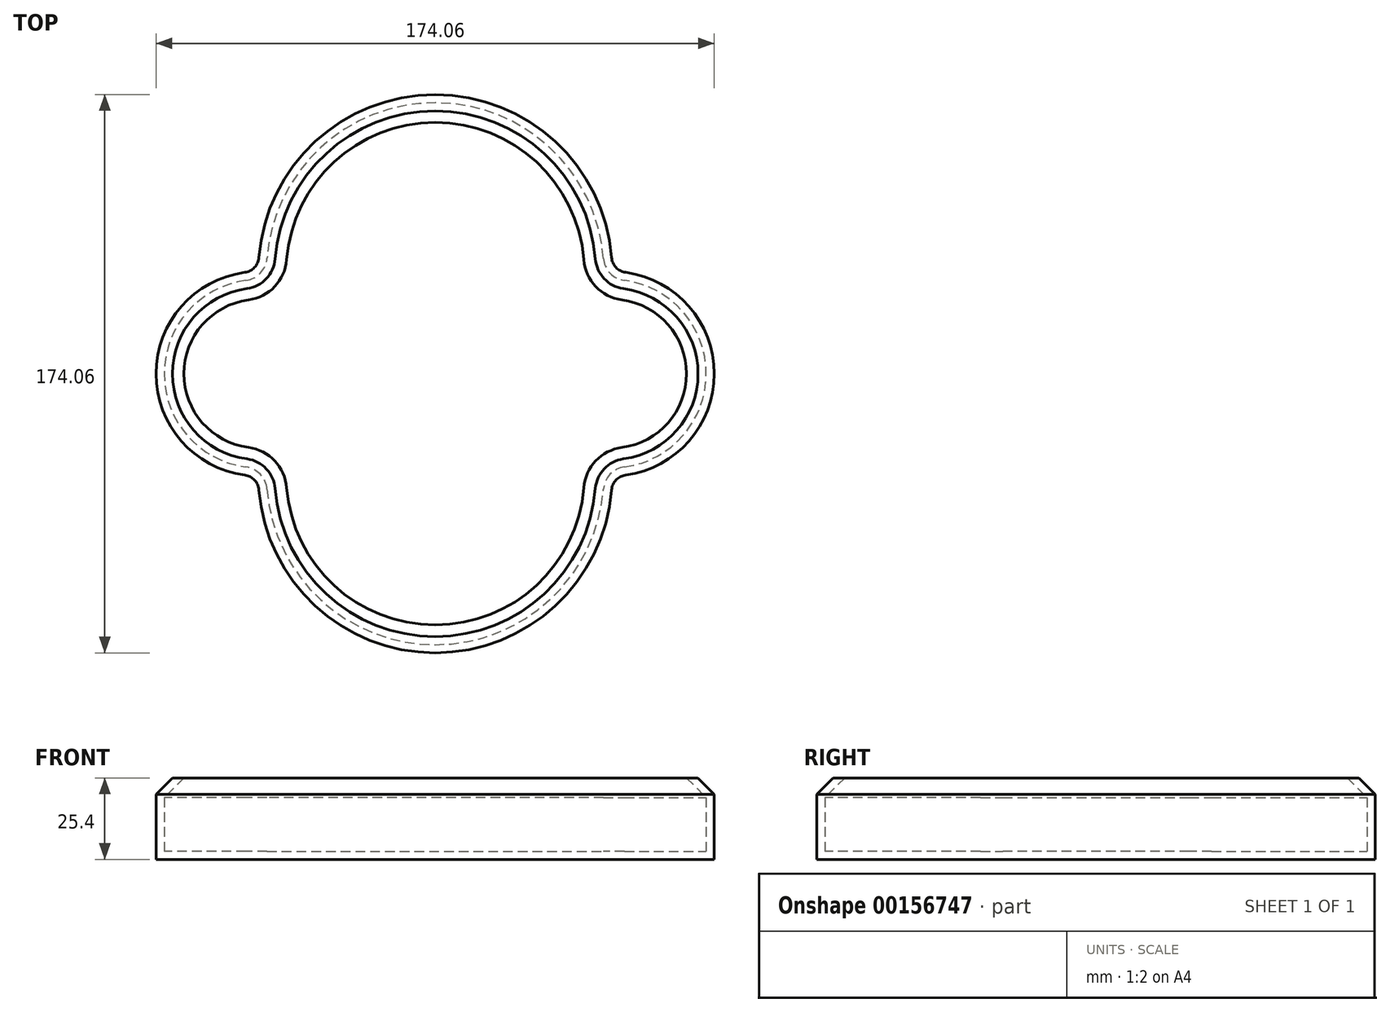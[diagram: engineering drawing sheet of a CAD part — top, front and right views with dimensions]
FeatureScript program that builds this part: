
annotation { "Feature Type Name" : "Feature", "Feature Type Description" : "" }
export const myFeature = defineFeature(function(context is Context, id is Id, definition is map)
    precondition{}
    {
        {
            var Q0;
            Q0=qCreatedBy(makeId("Top.planeOp"),FACE);
            var sketch = newSketch(context, id + "F0", { "sketchPlane" : qUnion([Q0])});
            skLineSegment(sketch, "E0.bottom", {"start": v(55.15, -31.88) * mm, "end": v(-55.15, -31.88) * mm});
            skLineSegment(sketch, "E0.top", {"start": v(55.15, 31.88) * mm, "end": v(-55.15, 31.88) * mm});
            skLineSegment(sketch, "E0.left", {"start": v(55.15, -31.88) * mm, "end": v(55.15, 31.88) * mm});
            skLineSegment(sketch, "E0.right", {"start": v(-55.15, -31.88) * mm, "end": v(-55.15, 31.88) * mm});
            skPoint(sketch, "E0.middle", {"position": v(0, 0) * mm});
            skArc(sketch, "E1", {"start": v(-55.15, 31.88) * mm, "mid": v(0, 87.03) * mm, "end": v(55.15, 31.88) * mm});
            skArc(sketch, "E2", {"start": v(-55.15, -31.88) * mm, "mid": v(-87.03, 0) * mm, "end": v(-55.15, 31.88) * mm});
            skArc(sketch, "E3", {"start": v(55.15, -31.88) * mm, "mid": v(87.03, 0) * mm, "end": v(55.15, 31.88) * mm});
            skArc(sketch, "E4", {"start": v(-55.15, -31.88) * mm, "mid": v(0, -87.03) * mm, "end": v(55.15, -31.88) * mm});
            skSolve(sketch);
        }
        {
            var Q0;
            Q0=makeQuery(id+"F0.imprint","IMPRINT",FACE,{"disambiguationData":[TD([[makeQuery(id+"F0.imprint","IMPRINT",EDGE,{"derivedFrom":sQuery(id+"F0.wireOp",EDGE,"E0.right")}),1.0]])]});
            var Q1;
            Q1=makeQuery(id+"F0.imprint","IMPRINT",FACE,{"disambiguationData":[TD([[makeQuery(id+"F0.imprint","IMPRINT",EDGE,{"derivedFrom":sQuery(id+"F0.wireOp",EDGE,"E0.top")}),-1.0]])]});
            var Q2;
            Q2=makeQuery(id+"F0.imprint","IMPRINT",FACE,{"disambiguationData":[TD([[makeQuery(id+"F0.imprint","IMPRINT",EDGE,{"derivedFrom":sQuery(id+"F0.wireOp",EDGE,"E0.left")}),-1.0]])]});
            var Q3;
            Q3=makeQuery(id+"F0.imprint","IMPRINT",FACE,{"disambiguationData":[TD([[makeQuery(id+"F0.imprint","IMPRINT",EDGE,{"derivedFrom":sQuery(id+"F0.wireOp",EDGE,"E0.bottom")}),1.0]])]});
            var Q4;
            Q4=makeQuery(id+"F0.imprint","IMPRINT",FACE,{"disambiguationData":[TD([[makeQuery(id+"F0.imprint","IMPRINT",EDGE,{"derivedFrom":sQuery(id+"F0.wireOp",EDGE,"E0.bottom")}),-1.0]])]});
            extrude(context, id + "F1", {"entities" : qUnion([Q0, Q1, Q2, Q3, Q4]), "endBound" : BoundingType.SYMMETRIC, "depth" : 25.4 * mm});
        }
        {
            var Q0;
            Q0=makeQuery(id+"F1.opExtrude","SWEPT_EDGE",EDGE,{"disambiguationData":[OSD([sQuery(id+"F0.wireOp",EDGE,"E0.bottom"),sQuery(id+"F0.wireOp",EDGE,"E0.left"),sQuery(id+"F0.wireOp",EDGE,"E3"),sQuery(id+"F0.wireOp",EDGE,"E4")])]});
            var Q1;
            Q1=makeQuery(id+"F1.opExtrude","SWEPT_EDGE",EDGE,{"disambiguationData":[OSD([sQuery(id+"F0.wireOp",EDGE,"E0.top"),sQuery(id+"F0.wireOp",EDGE,"E0.left"),sQuery(id+"F0.wireOp",EDGE,"E1"),sQuery(id+"F0.wireOp",EDGE,"E3")])]});
            var Q2;
            Q2=makeQuery(id+"F1.opExtrude","SWEPT_EDGE",EDGE,{"disambiguationData":[OSD([sQuery(id+"F0.wireOp",EDGE,"E0.top"),sQuery(id+"F0.wireOp",EDGE,"E0.right"),sQuery(id+"F0.wireOp",EDGE,"E1"),sQuery(id+"F0.wireOp",EDGE,"E2")])]});
            var Q3;
            Q3=makeQuery(id+"F1.opExtrude","SWEPT_EDGE",EDGE,{"disambiguationData":[OSD([sQuery(id+"F0.wireOp",EDGE,"E0.bottom"),sQuery(id+"F0.wireOp",EDGE,"E0.right"),sQuery(id+"F0.wireOp",EDGE,"E2"),sQuery(id+"F0.wireOp",EDGE,"E4")])]});
            fillet(context, id + "F2", {"entities" : qUnion([Q0, Q1, Q2, Q3]), "radius" : 5.08 * mm, "tangentPropagation" : true, "allowEdgeOverflow" : false});
        }
        {
            var Q0;
            Q0=makeQuery(id+"F1.opExtrude","CAP_EDGE",EDGE,{"disambiguationData":[OSD([sQuery(id+"F0.wireOp",EDGE,"E3")])],"isStart":false});
            var Q1;
            Q1=makeQuery(id+"F1.opExtrude","CAP_EDGE",EDGE,{"disambiguationData":[OSD([sQuery(id+"F0.wireOp",EDGE,"E4")])],"isStart":false});
            var Q2;
            Q2=makeQuery(id+"F1.opExtrude","CAP_EDGE",EDGE,{"disambiguationData":[OSD([sQuery(id+"F0.wireOp",EDGE,"E1")])],"isStart":false});
            var Q3;
            Q3=makeQuery(id+"F1.opExtrude","CAP_EDGE",EDGE,{"disambiguationData":[OSD([sQuery(id+"F0.wireOp",EDGE,"E2")])],"isStart":false});
            var Q4;
            {var subQ0=sQuery(id+"F0.wireOp",EDGE,"E2");var subQ1=sQuery(id+"F0.wireOp",EDGE,"E1");Q4=makeQuery(id+"F2.opFillet","BLEND_EDGE",EDGE,{"blendedFrom":[makeQuery(id+"F1.opExtrude","SWEPT_EDGE",EDGE,{"disambiguationData":[OSD([sQuery(id+"F0.wireOp",EDGE,"E0.top"),sQuery(id+"F0.wireOp",EDGE,"E0.right"),subQ1,subQ0])]}),makeQuery(id+"F1.opExtrude","CAP_FACE",FACE,{"disambiguationData":[OSD([subQ1,subQ0,sQuery(id+"F0.wireOp",EDGE,"E3"),sQuery(id+"F0.wireOp",EDGE,"E4")])],"isStart":false})],"blendedInto":[makeQuery(id+"F1.opExtrude","CAP_FACE",FACE,{"disambiguationData":[OSD([subQ1,subQ0,sQuery(id+"F0.wireOp",EDGE,"E3"),sQuery(id+"F0.wireOp",EDGE,"E4")])],"isStart":false})]});}
            var Q5;
            {var subQ0=sQuery(id+"F0.wireOp",EDGE,"E4");var subQ1=sQuery(id+"F0.wireOp",EDGE,"E2");Q5=makeQuery(id+"F2.opFillet","BLEND_EDGE",EDGE,{"blendedFrom":[makeQuery(id+"F1.opExtrude","SWEPT_EDGE",EDGE,{"disambiguationData":[OSD([sQuery(id+"F0.wireOp",EDGE,"E0.bottom"),sQuery(id+"F0.wireOp",EDGE,"E0.right"),subQ1,subQ0])]}),makeQuery(id+"F1.opExtrude","CAP_FACE",FACE,{"disambiguationData":[OSD([sQuery(id+"F0.wireOp",EDGE,"E1"),subQ1,sQuery(id+"F0.wireOp",EDGE,"E3"),subQ0])],"isStart":false})],"blendedInto":[makeQuery(id+"F1.opExtrude","CAP_FACE",FACE,{"disambiguationData":[OSD([sQuery(id+"F0.wireOp",EDGE,"E1"),subQ1,sQuery(id+"F0.wireOp",EDGE,"E3"),subQ0])],"isStart":false})]});}
            var Q6;
            {var subQ0=sQuery(id+"F0.wireOp",EDGE,"E4");var subQ1=sQuery(id+"F0.wireOp",EDGE,"E3");Q6=makeQuery(id+"F2.opFillet","BLEND_EDGE",EDGE,{"blendedFrom":[makeQuery(id+"F1.opExtrude","SWEPT_EDGE",EDGE,{"disambiguationData":[OSD([sQuery(id+"F0.wireOp",EDGE,"E0.bottom"),sQuery(id+"F0.wireOp",EDGE,"E0.left"),subQ1,subQ0])]}),makeQuery(id+"F1.opExtrude","CAP_FACE",FACE,{"disambiguationData":[OSD([sQuery(id+"F0.wireOp",EDGE,"E1"),sQuery(id+"F0.wireOp",EDGE,"E2"),subQ1,subQ0])],"isStart":false})],"blendedInto":[makeQuery(id+"F1.opExtrude","CAP_FACE",FACE,{"disambiguationData":[OSD([sQuery(id+"F0.wireOp",EDGE,"E1"),sQuery(id+"F0.wireOp",EDGE,"E2"),subQ1,subQ0])],"isStart":false})]});}
            var Q7;
            {var subQ0=sQuery(id+"F0.wireOp",EDGE,"E3");var subQ1=sQuery(id+"F0.wireOp",EDGE,"E1");Q7=makeQuery(id+"F2.opFillet","BLEND_EDGE",EDGE,{"blendedFrom":[makeQuery(id+"F1.opExtrude","SWEPT_EDGE",EDGE,{"disambiguationData":[OSD([sQuery(id+"F0.wireOp",EDGE,"E0.top"),sQuery(id+"F0.wireOp",EDGE,"E0.left"),subQ1,subQ0])]}),makeQuery(id+"F1.opExtrude","CAP_FACE",FACE,{"disambiguationData":[OSD([subQ1,sQuery(id+"F0.wireOp",EDGE,"E2"),subQ0,sQuery(id+"F0.wireOp",EDGE,"E4")])],"isStart":false})],"blendedInto":[makeQuery(id+"F1.opExtrude","CAP_FACE",FACE,{"disambiguationData":[OSD([subQ1,sQuery(id+"F0.wireOp",EDGE,"E2"),subQ0,sQuery(id+"F0.wireOp",EDGE,"E4")])],"isStart":false})]});}
            chamfer(context, id + "F3", {"entities" : qUnion([Q0, Q1, Q2, Q3, Q4, Q5, Q6, Q7]), "width" : 5.08 * mm, "tangentPropagation" : true});
        }
        {
            var Q0;
            Q0=makeQuery(id+"F1.opExtrude","CAP_FACE",FACE,{"disambiguationData":[OSD([sQuery(id+"F0.wireOp",EDGE,"E1"),sQuery(id+"F0.wireOp",EDGE,"E2"),sQuery(id+"F0.wireOp",EDGE,"E3"),sQuery(id+"F0.wireOp",EDGE,"E4")])],"isStart":false});
            shell(context, id + "F4", {"entities" : qUnion([Q0]), "thickness" : 2.54 * mm});
        }
    });
